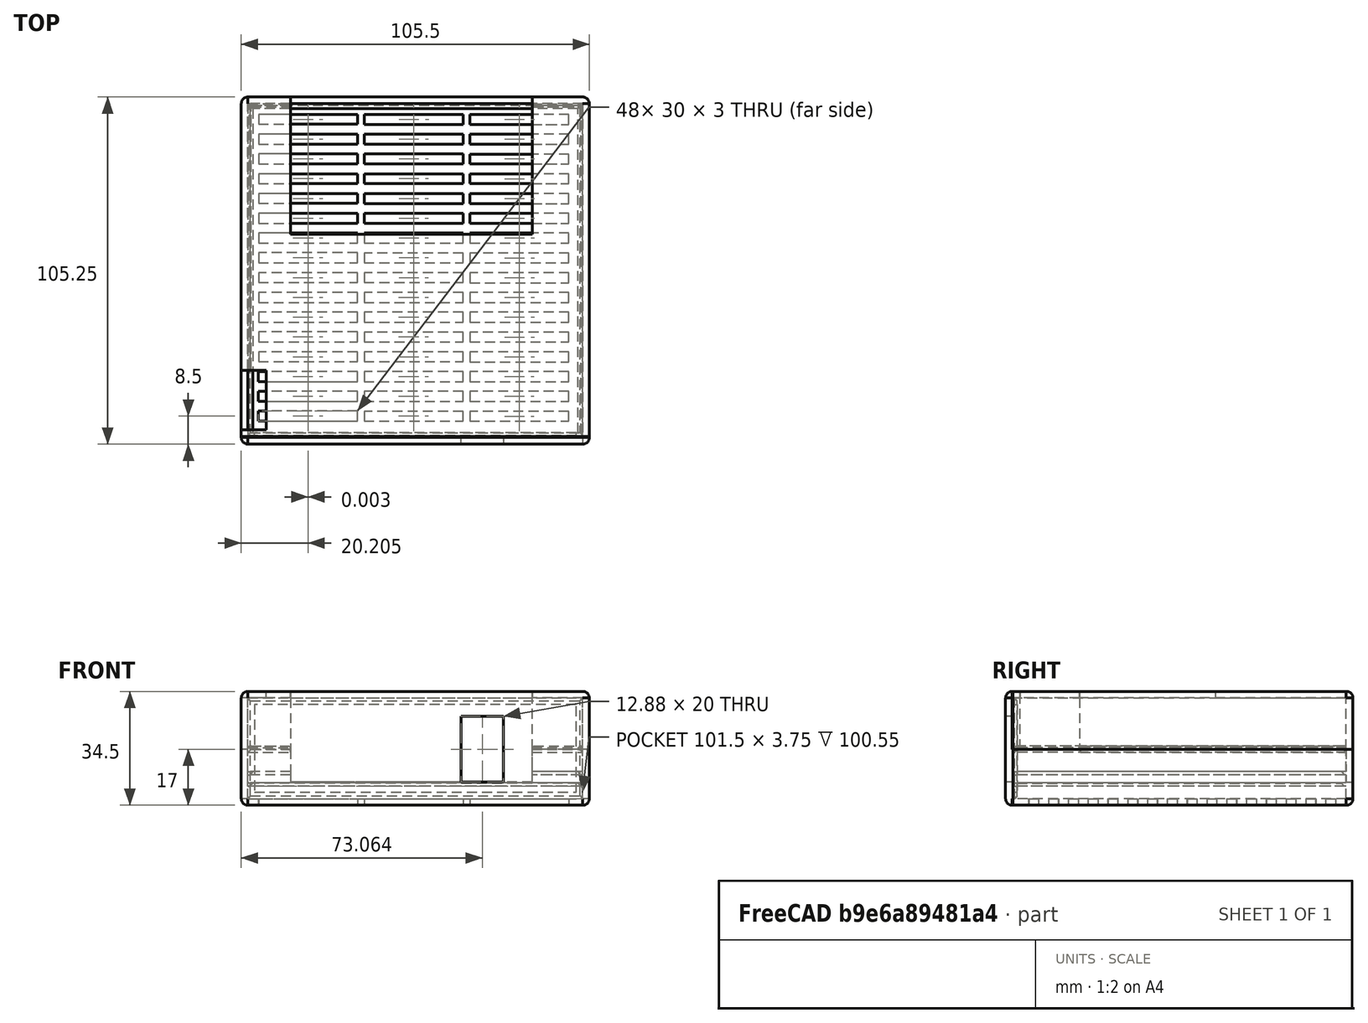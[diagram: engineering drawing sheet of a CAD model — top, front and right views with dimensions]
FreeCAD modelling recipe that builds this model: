
FCSTD DOCUMENT  (FreeCAD 2021.1015R24301 +4280 (Git))
Label: Box
License: All rights reserved
objects: Sketcher::SketchObject×9, PartDesign::SubShapeBinder×6, PartDesign::Pad×5, PartDesign::Pocket×4, PartDesign::Chamfer×3, PartDesign::Body×3, Mesh::Feature×3, PartDesign::Thickness×2, PartDesign::Boolean×2, PartDesign::Solid×2, Mesh::FeatureCustom×1, Spreadsheet::Sheet×1, PartDesign::LinearPattern×1, PartDesign::Split×1
note: 71 computed .brp shape members not serialized (recipe doc carries the construction recipe); baked Part::Feature solids carry a one-line shape summary decoded from their .brp

FEATURE [Mesh::FeatureCustom] OBJ_PCB_BanFlow
  Placement = pos=(-1025.77,1010.73,0) rot=(0,0,1;0rad)
FEATURE [Sketcher::SketchObject] Sketch
  AttachmentOffset = pos=(-0.25,0,-5) rot=(0,0,1;0rad)
  FullyConstrained = true
  MapMode = 5
  Placement = pos=(-0.25,0,-5) rot=(0,0,1;0rad)
  Support = -> [XY_Plane]
  expr: AttachmentOffset.Base.x = -<<Parameters>>.clearance
  expr: AttachmentOffset.Base.z = -<<Parameters>>.PCBLowClearance
  expr: Constraints[10] = <<Parameters>>.PCBwidth + 2 * <<Parameters>>.clearance
  expr: Constraints[9] = <<Parameters>>.PCBwidth + <<Parameters>>.clearance
  sketch-geometry (4):
    g0: LineSegment StartX=0 StartY=0 StartZ=0 EndX=101.5 EndY=0 EndZ=0
    g1: LineSegment StartX=101.5 StartY=0 StartZ=0 EndX=101.5 EndY=101.25 EndZ=0
    g2: LineSegment StartX=101.5 StartY=101.25 StartZ=0 EndX=0 EndY=101.25 EndZ=0
    g3: LineSegment StartX=0 StartY=101.25 StartZ=0 EndX=0 EndY=0 EndZ=0
  constraints (11):
    c: Coincident(g0,g1)
    c: Coincident(g1,g2)
    c: Coincident(g2,g3)
    c: Coincident(g3,g0)
    c: Horizontal(g0)
    c: Horizontal(g2)
    c: Vertical(g1)
    c: Vertical(g3)
    c: Coincident(g0,g-1)
    c: DistanceY(g1,g1) = 101.25
    c: DistanceX(g0,g0) = 101.5
FEATURE [PartDesign::Pad] Pad
  AddSubType = 0
  CheckUpToFaceLimits = true
  ClaimChildren = false
  Direction = (1,1,1)
  Fit = 0
  FitJoin = 0
  InnerFit = 0
  InnerFitJoin = 0
  InnerTaperAngle = 0
  InnerTaperAngleRev = 0
  Length = 30.5
  Length2 = 100
  Linearize = true
  NewSolid = false
  Profile = -> Sketch
  Suppress = false
  Type = 0
  _ProfileBasedVersion = 1
  expr: Length = <<Parameters>>.CaseInsideHeight
FEATURE [PartDesign::Thickness] Thickness
  AddSubType = 0
  Base = -> Pad [Face1]
  BaseFeature = -> Pad
  Intersection = false
  Join = 0
  Mode = 0
  NewSolid = false
  SupportTransform = false
  Suppress = false
  Value = 2
  expr: Value = <<Parameters>>.CaseThickness
FEATURE [Spreadsheet::Sheet] Spreadsheet  label="Parameters"
  PythonMode = false
  cells = A1='clearance; B1(clearance)=0.25; C1='mm; A2='PCB; B2(PCBwidth)=101; C2='mm; A3='PCBLowClearance; B3(PCBLowClearance)=5; C3='mm; A4='PCBHighClearance; B4(PCBHighClearance)=22; C4='mm; A5=PCB thickness; B5(PCBThickness)=3; C5='mm; A6=Case Thickness; B6(CaseThickness)=2; C6='mm; A7=Case inside height; B7(CaseInsideHeight)==PCBThickness + PCBLowClearance + PCBHighClearance + clearance * 2; C7='mm; D7=Clearance is included for PCB holder rails; A8='ShelfWidth; B8(ShelfWidth)=1.5; C8='mm; A9='ShelfThickness; B9(ShelfThickness)=1; C9='mm
FEATURE [PartDesign::SubShapeBinder] Binder  label="Binder(Thickness)..."
  BindCopyOnChange = 0
  BindMode = 0
  ClaimChildren = false
  Context = -> Body001 [Binder.]
  FillStyle = 0
  Fuse = false
  MakeFace = true
  PartialLoad = false
  Relative = true
  Support = -> [Body[Thickness.Edge12,Thickness.Edge8,Thickness.Edge11,Thickness.Edge1]]
  _Version = 8
FEATURE [PartDesign::Pad] Pad001
  AddSubType = 0
  CheckUpToFaceLimits = true
  ClaimChildren = false
  Direction = (1,1,1)
  Fit = 0
  FitJoin = 0
  InnerFit = 0
  InnerFitJoin = 0
  InnerTaperAngle = 0
  InnerTaperAngleRev = 0
  Length = 0.25
  Length2 = 100
  Linearize = true
  NewSolid = false
  Profile = -> Binder
  Suppress = false
  Type = 0
  _ProfileBasedVersion = 1
  expr: Length = <<Parameters>>.clearance
FEATURE [PartDesign::Thickness] Thickness001
  AddSubType = 0
  Base = -> Pad001 [Face6]
  BaseFeature = -> Pad001
  Intersection = false
  Join = 0
  Mode = 0
  NewSolid = false
  SupportTransform = false
  Suppress = false
  Value = 2
  expr: Value = <<Parameters>>.CaseThickness
FEATURE [Sketcher::SketchObject] Sketch001
  AttachmentOffset = pos=(-0.5,0,-0.25) rot=(0,0,1;0rad)
  FullyConstrained = true
  MapMode = 5
  Placement = pos=(-0.5,0,-0.25) rot=(0,0,1;0rad)
  Support = -> [XY_Plane]
  expr: AttachmentOffset.Base.x = -<<Parameters>>.clearance * 2
  expr: AttachmentOffset.Base.z = -<<Parameters>>.clearance
  expr: Constraints[19] = <<Parameters>>.ShelfWidth + <<Parameters>>.clearance
  expr: Constraints[20] = <<Parameters>>.PCBwidth + 2 * <<Parameters>>.clearance
  expr: Constraints[21] = <<Parameters>>.ShelfWidth + <<Parameters>>.clearance
  expr: Constraints[22] = <<Parameters>>.PCBwidth + <<Parameters>>.clearance * 4
  sketch-geometry (8):
    g0: LineSegment StartX=0 StartY=0 StartZ=0 EndX=0 EndY=101.5 EndZ=0
    g1: LineSegment StartX=0 StartY=101.5 StartZ=0 EndX=102 EndY=101.5 EndZ=0
    g2: LineSegment StartX=102 StartY=101.5 StartZ=0 EndX=102 EndY=0 EndZ=0
    g3: LineSegment StartX=102 StartY=3e-15 StartZ=0 EndX=100.25 EndY=3e-15 EndZ=0
    g4: LineSegment StartX=100.25 StartY=3e-15 StartZ=0 EndX=100.25 EndY=99.75 EndZ=0
    g5: LineSegment StartX=100.25 StartY=99.75 StartZ=0 EndX=1.75 EndY=99.75 EndZ=0
    g6: LineSegment StartX=1.75 StartY=99.75 StartZ=0 EndX=1.75 EndY=0 EndZ=0
    g7: LineSegment StartX=1.75 StartY=0 StartZ=0 EndX=0 EndY=0 EndZ=0
  constraints (23):
    c: Coincident(g0,g-1)
    c: PointOnObject(g0,g-2)
    c: Coincident(g1,g0)
    c: Horizontal(g1)
    c: Vertical(g2)
    c: Horizontal(g3)
    c: Coincident(g4,g3)
    c: Vertical(g4)
    c: Horizontal(g5)
    c: Coincident(g6,g5)
    c: Vertical(g6)
    c: Coincident(g7,g6)
    c: Coincident(g7,g0)
    c: Horizontal(g7)
    c: Equal(g7,g3)
    c: Equal(g6,g4)
    c: Coincident(g5,g4)
    c: Coincident(g3,g2)
    c: Coincident(g2,g1)
    c: DistanceY(g4,g1) = 1.75
    c: DistanceY(g0,g0) = 101.5
    c: DistanceX(g7,g7) = 1.75
    c: DistanceX(g1,g1) = 102
FEATURE [PartDesign::Pad] Pad002
  AddSubType = 0
  BaseFeature = -> Thickness
  CheckUpToFaceLimits = true
  ClaimChildren = false
  Direction = (1,1,1)
  Fit = 0
  FitJoin = 0
  InnerFit = 0
  InnerFitJoin = 0
  InnerTaperAngle = 0
  InnerTaperAngleRev = 0
  Length = 1
  Length2 = 100
  Linearize = true
  NewSolid = false
  Profile = -> Sketch001
  Reversed = true
  Suppress = false
  Type = 0
  _ProfileBasedVersion = 1
  expr: Length = <<Parameters>>.ShelfThickness
FEATURE [PartDesign::LinearPattern] LinearPattern
  AddSubType = 0
  BaseFeature = -> Pad002
  CopyShape = false
  Direction = -> Sketch001 [N_Axis]
  Length = 3.5
  NewSolid = false
  Occurrences = 2
  OriginalSubs = -> [Pad002]
  Originals = -> [Pad002]
  ParallelTransform = true
  SubTransform = true
  Suppress = false
  _Version = 3
  expr: Length = <<Parameters>>.PCBThickness + 2 * <<Parameters>>.clearance
FEATURE [Sketcher::SketchObject] Sketch002
  AttachmentOffset = pos=(0,0,10) rot=(0,0,1;0rad)
  FullyConstrained = false
  MapMode = 5
  Placement = pos=(0,0,10) rot=(0,0,1;0rad)
  Support = -> [XY_Plane]
  sketch-geometry (4):
    g0: LineSegment StartX=-6.24338 StartY=2.38313 StartZ=0 EndX=5.37009 EndY=2.38313 EndZ=0
    g1: LineSegment StartX=5.37009 StartY=2.38313 StartZ=0 EndX=5.37009 EndY=20.3657 EndZ=0
    g2: LineSegment StartX=5.37009 StartY=20.3657 StartZ=0 EndX=-6.24338 EndY=20.3657 EndZ=0
    g3: LineSegment StartX=-6.24338 StartY=20.3657 StartZ=0 EndX=-6.24338 EndY=2.38313 EndZ=0
  constraints (8):
    c: Coincident(g0,g1)
    c: Coincident(g1,g2)
    c: Coincident(g2,g3)
    c: Coincident(g3,g0)
    c: Horizontal(g0)
    c: Horizontal(g2)
    c: Vertical(g1)
    c: Vertical(g3)
FEATURE [PartDesign::Pocket] Pocket
  AddSubType = 1
  BaseFeature = -> LinearPattern
  CheckUpToFaceLimits = true
  ClaimChildren = false
  Fit = 0
  FitJoin = 0
  InnerFit = 0
  InnerFitJoin = 0
  InnerTaperAngle = 0
  InnerTaperAngleRev = 0
  Length = 5
  Length2 = 100
  Linearize = true
  NewSolid = false
  Profile = -> Sketch002
  Reversed = true
  Suppress = false
  Type = 1
  _ProfileBasedVersion = 1
  _Version = 1
FEATURE [Sketcher::SketchObject] Sketch003
  FullyConstrained = false
  MapMode = 5
  Support = -> [XY_Plane]
  sketch-geometry (4):
    g0: LineSegment StartX=12.6327 StartY=103.802 StartZ=0 EndX=85.9095 EndY=103.802 EndZ=0
    g1: LineSegment StartX=85.9095 StartY=103.802 StartZ=0 EndX=85.9095 EndY=61.6576 EndZ=0
    g2: LineSegment StartX=85.9095 StartY=61.6576 StartZ=0 EndX=12.6327 EndY=61.6576 EndZ=0
    g3: LineSegment StartX=12.6327 StartY=61.6576 StartZ=0 EndX=12.6327 EndY=103.802 EndZ=0
  constraints (8):
    c: Coincident(g0,g1)
    c: Coincident(g1,g2)
    c: Coincident(g2,g3)
    c: Coincident(g3,g0)
    c: Horizontal(g0)
    c: Horizontal(g2)
    c: Vertical(g1)
    c: Vertical(g3)
FEATURE [PartDesign::Pocket] Pocket001
  AddSubType = 1
  BaseFeature = -> Pocket
  CheckUpToFaceLimits = true
  ClaimChildren = false
  Fit = 0
  FitJoin = 0
  InnerFit = 0
  InnerFitJoin = 0
  InnerTaperAngle = 0
  InnerTaperAngleRev = 0
  Length = 5
  Length2 = 100
  Linearize = true
  NewSolid = false
  Profile = -> Sketch003
  Reversed = true
  Suppress = false
  Type = 1
  _ProfileBasedVersion = 1
  _Version = 1
FEATURE [Sketcher::SketchObject] Sketch005
  FullyConstrained = false
  MapMode = 5
  Support = -> [XY_Plane001]
  sketch-geometry (4):
    g0: LineSegment StartX=64.3744 StartY=20.9694 StartZ=0 EndX=77.2533 EndY=20.9694 EndZ=0
    g1: LineSegment StartX=77.2533 StartY=20.9694 StartZ=0 EndX=77.2533 EndY=-4.03701 EndZ=0
    g2: LineSegment StartX=77.2533 StartY=-4.03701 StartZ=0 EndX=64.3744 EndY=-4.03701 EndZ=0
    g3: LineSegment StartX=64.3744 StartY=-4.03701 StartZ=0 EndX=64.3744 EndY=20.9694 EndZ=0
  constraints (8):
    c: Coincident(g0,g1)
    c: Coincident(g1,g2)
    c: Coincident(g2,g3)
    c: Coincident(g3,g0)
    c: Horizontal(g0)
    c: Horizontal(g2)
    c: Vertical(g1)
    c: Vertical(g3)
FEATURE [PartDesign::Pocket] Pocket002
  AddSubType = 1
  BaseFeature = -> Thickness001
  CheckUpToFaceLimits = true
  ClaimChildren = false
  Fit = 0
  FitJoin = 0
  InnerFit = 0
  InnerFitJoin = 0
  InnerTaperAngle = 0
  InnerTaperAngleRev = 0
  Length = 20
  Length2 = 100
  Linearize = true
  NewSolid = false
  Profile = -> Sketch005
  Reversed = true
  Suppress = false
  Type = 0
  _ProfileBasedVersion = 1
  _Version = 1
FEATURE [Sketcher::SketchObject] Sketch006
  AttachmentOffset = pos=(0,0,10) rot=(0,0,1;0rad)
  FullyConstrained = false
  MapMode = 5
  Placement = pos=(0,0,10) rot=(0,0,1;0rad)
  Support = -> [XY_Plane]
  sketch-geometry (4):
    g0: LineSegment StartX=-6.43563 StartY=105.494 StartZ=0 EndX=106.904 EndY=105.494 EndZ=0
    g1: LineSegment StartX=106.904 StartY=105.494 StartZ=0 EndX=106.904 EndY=-7.55383 EndZ=0
    g2: LineSegment StartX=106.904 StartY=-7.55383 StartZ=0 EndX=-6.43563 EndY=-7.55383 EndZ=0
    g3: LineSegment StartX=-6.43563 StartY=-7.55383 StartZ=0 EndX=-6.43563 EndY=105.494 EndZ=0
  constraints (8):
    c: Coincident(g0,g1)
    c: Coincident(g1,g2)
    c: Coincident(g2,g3)
    c: Coincident(g3,g0)
    c: Horizontal(g0)
    c: Horizontal(g2)
    c: Vertical(g1)
    c: Vertical(g3)
FEATURE [PartDesign::SubShapeBinder] Binder001  label="Binder001(Sketch006)"
  BindCopyOnChange = 0
  BindMode = 0
  ClaimChildren = false
  Context = -> Body [Binder001.]
  FillStyle = 0
  Fuse = false
  MakeFace = true
  PartialLoad = false
  Relative = true
  Support = -> [Sketch006]
  _Version = 8
FEATURE [Sketcher::SketchObject] Sketch007
  AttachmentOffset = pos=(0,0,9) rot=(0,0,1;0rad)
  FullyConstrained = false
  MapMode = 5
  Placement = pos=(0,0,9) rot=(0,0,1;0rad)
  Support = -> [XY_Plane]
  expr: Constraints[29] = <<Parameters>>.clearance
  expr: Constraints[30] = <<Parameters>>.PCBwidth + <<Parameters>>.clearance
  expr: Constraints[32] = <<Parameters>>.PCBwidth + <<Parameters>>.clearance
  sketch-geometry (12):
    g0: LineSegment StartX=0.75 StartY=20.7074 StartZ=0 EndX=0.75 EndY=100.25 EndZ=0
    g1: LineSegment StartX=0.75 StartY=100.25 StartZ=0 EndX=12.6277 EndY=100.25 EndZ=0
    g2: LineSegment StartX=12.6277 StartY=100.25 StartZ=0 EndX=12.6277 EndY=101.25 EndZ=0
    g3: LineSegment StartX=85.9129 StartY=101.25 StartZ=0 EndX=85.9129 EndY=100.25 EndZ=0
    g4: LineSegment StartX=85.9129 StartY=100.25 StartZ=0 EndX=100.25 EndY=100.25 EndZ=0
    g5: LineSegment StartX=100.25 StartY=100.25 StartZ=0 EndX=100.25 EndY=0 EndZ=0
    g6: LineSegment StartX=0.75 StartY=20.7074 StartZ=0 EndX=-0.25 EndY=20.7074 EndZ=0
    g7: LineSegment StartX=-0.25 StartY=20.7074 StartZ=0 EndX=-0.25 EndY=101.25 EndZ=0
    g8: LineSegment StartX=-0.25 StartY=101.25 StartZ=0 EndX=12.6277 EndY=101.25 EndZ=0
    g9: LineSegment StartX=85.9129 StartY=101.25 StartZ=0 EndX=101.25 EndY=101.25 EndZ=0
    g10: LineSegment StartX=101.25 StartY=101.25 StartZ=0 EndX=101.25 EndY=0 EndZ=0
    g11: LineSegment StartX=101.25 StartY=0 StartZ=0 EndX=100.25 EndY=0 EndZ=0
  constraints (33):
    c: Vertical(g0)
    c: Coincident(g1,g0)
    c: Horizontal(g1)
    c: Coincident(g2,g1)
    c: Vertical(g2)
    c: Vertical(g3)
    c: Horizontal(g4)
    c: Coincident(g5,g4)
    c: Vertical(g5)
    c: Equal(g3,g2)
    c: Coincident(g4,g3)
    c: Coincident(g6,g0)
    c: Horizontal(g6)
    c: Coincident(g7,g6)
    c: Vertical(g7)
    c: Coincident(g8,g7)
    c: Coincident(g8,g2)
    c: Horizontal(g8)
    c: Coincident(g9,g3)
    c: Horizontal(g9)
    c: Coincident(g10,g9)
    c: Vertical(g10)
    c: Coincident(g11,g10)
    c: Coincident(g11,g5)
    c: Horizontal(g11)
    c: Equal(g6,g11)
    c: Equal(g11,g3)
    c: DistanceY(g2,g3) = 0
    c: DistanceX(g6,g6) = 1
    c: DistanceX(g6,g-1) = 0.25
    c: DistanceX(g-1,g10) = 101.25
    c: PointOnObject(g10,g-1)
    c: DistanceY(g10,g10) = 101.25
FEATURE [PartDesign::Pad] Pad003
  AddSubType = 0
  CheckUpToFaceLimits = true
  ClaimChildren = false
  Direction = (1,1,1)
  Fit = 0
  FitJoin = 0
  InnerFit = 0
  InnerFitJoin = 0
  InnerTaperAngle = 0
  InnerTaperAngleRev = 0
  Length = 2
  Length2 = 100
  Linearize = true
  NewSolid = false
  Profile = -> Sketch007
  Suppress = false
  Type = 0
  _ProfileBasedVersion = 1
FEATURE [PartDesign::SubShapeBinder] Binder002  label="Binder002(Split_i0)..."
  BindCopyOnChange = 0
  BindMode = 0
  ClaimChildren = false
  Context = -> Body003 [Binder002.]
  FillStyle = 0
  Fuse = true
  MakeFace = true
  PartialLoad = false
  Relative = true
  Support = -> [Body[Split_i0.],Pad003]
  _Version = 8
FEATURE [PartDesign::SubShapeBinder] Reference002  label="Reference002(Pad003)"
  BindCopyOnChange = 0
  BindMode = 0
  ClaimChildren = false
  Context = -> Body003 [Reference002.]
  FillStyle = 0
  Fuse = false
  MakeFace = true
  PartialLoad = false
  Relative = true
  Support = -> [Pad003]
  _Version = 8
FEATURE [PartDesign::SubShapeBinder] Reference003  label="Reference003(*Split_i0...)"
  BindCopyOnChange = 0
  BindMode = 0
  ClaimChildren = false
  Context = -> Body003 [Reference003.]
  FillStyle = 0
  Fuse = false
  MakeFace = true
  PartialLoad = false
  Relative = true
  Support = -> [Binder002]
  _Version = 8
FEATURE [PartDesign::Boolean] Boolean
  ExportMode = 0
  Group = -> [Reference002,Reference003]
  NewSolid = true
  Suppress = false
  Type = 0
  _ExportChildren = -> [Reference002,Reference003]
  _GroupVersion = 1
FEATURE [Sketcher::SketchObject] Sketch008
  ExternalGeometry = -> [Pocket002]
  FullyConstrained = true
  MapMode = 5
  Placement = pos=(0,0,0) rot=(0,0.707107,0.707107;3.14159rad)
  Support = -> [Pocket002]
  sketch-geometry (4):
    g0: LineSegment StartX=-99.25 StartY=23.5 StartZ=0 EndX=-1.75 EndY=23.5 EndZ=0
    g1: LineSegment StartX=-1.75 StartY=23.5 StartZ=0 EndX=-1.75 EndY=-3 EndZ=0
    g2: LineSegment StartX=-1.75 StartY=-3 StartZ=0 EndX=-99.25 EndY=-3 EndZ=0
    g3: LineSegment StartX=-99.25 StartY=-3 StartZ=0 EndX=-99.25 EndY=23.5 EndZ=0
  constraints (12):
    c: Coincident(g0,g1)
    c: Coincident(g1,g2)
    c: Coincident(g2,g3)
    c: Coincident(g3,g0)
    c: Horizontal(g0)
    c: Horizontal(g2)
    c: Vertical(g1)
    c: Vertical(g3)
    c: DistanceY(g0,g-6) = 2
    c: DistanceX(g0,g-6) = 2
    c: DistanceY(g-5,g2) = 2
    c: DistanceX(g-5,g2) = 2
FEATURE [PartDesign::Pad] Pad004
  AddSubType = 0
  BaseFeature = -> Pocket002
  CheckUpToFaceLimits = true
  ClaimChildren = false
  Direction = (1,1,1)
  Fit = 0
  FitJoin = 0
  InnerFit = 0
  InnerFitJoin = 0
  InnerTaperAngle = 0
  InnerTaperAngleRev = 0
  Length = 1.5
  Length2 = 100
  Linearize = true
  NewSolid = false
  Profile = -> Sketch008
  Suppress = false
  Type = 0
  _ProfileBasedVersion = 1
FEATURE [PartDesign::Chamfer] Chamfer
  AddSubType = 0
  Angle = 45
  Base = -> Pad004 [Edge25,Edge26,Edge27,Edge28]
  BaseFeature = -> Pad004
  ChamferType = 0
  FlipDirection = false
  NewSolid = false
  Size = 0.8
  Size2 = 1
  SupportTransform = false
  Suppress = false
FEATURE [PartDesign::Body] Body001  label="SideDoor"
  AutoGroupSolids = false
  ExportMode = 0
  Group = -> [Binder,Pad001,Thickness001,Sketch005,Pocket002,Sketch008,Pad004,Chamfer]
  Origin = -> Origin001
  Tip = -> Chamfer
  _ExportChildren = -> [Pad001,Thickness001,Pocket002,Pad004,Chamfer]
  _GroupVersion = 1
FEATURE [PartDesign::SubShapeBinder] Reference  label="Reference(SideDoor)"
  BindCopyOnChange = 0
  BindMode = 0
  ClaimChildren = false
  Context = -> Body003 [Reference.]
  FillStyle = 0
  Fuse = false
  MakeFace = true
  PartialLoad = false
  Relative = true
  Support = -> [Body001]
  _Version = 8
FEATURE [PartDesign::Boolean] Boolean001
  BaseFeature = -> Boolean
  ExportMode = 0
  Group = -> [Reference]
  NewSolid = false
  Suppress = false
  Type = 1
  _ExportChildren = -> [Reference]
  _GroupVersion = 1
FEATURE [Sketcher::SketchObject] Sketch009
  FullyConstrained = true
  MapMode = 5
  Support = -> [XY_Plane003]
  expr: Constraints[10] = <<Parameters>>.PCBwidth - 3mm
  sketch-geometry (239):
    g0: LineSegment StartX=3 StartY=95 StartZ=0 EndX=33 EndY=95 EndZ=0
    g1: LineSegment StartX=33 StartY=95 StartZ=0 EndX=33 EndY=98 EndZ=0
    g2: LineSegment StartX=33 StartY=98 StartZ=0 EndX=3 EndY=98 EndZ=0
    g3: LineSegment StartX=3 StartY=98 StartZ=0 EndX=3 EndY=95 EndZ=0
    g4: LineSegment StartX=35.033 StartY=94.9839 StartZ=0 EndX=65.033 EndY=94.9839 EndZ=0
    g5: LineSegment StartX=65.033 StartY=94.9839 StartZ=0 EndX=65.033 EndY=97.9839 EndZ=0
    g6: LineSegment StartX=65.033 StartY=97.9839 StartZ=0 EndX=35.033 EndY=97.9839 EndZ=0
    g7: LineSegment StartX=35.033 StartY=97.9839 StartZ=0 EndX=35.033 EndY=94.9839 EndZ=0
    g8: LineSegment [constr] StartX=3 StartY=95 StartZ=0 EndX=35.033 EndY=94.9839 EndZ=0
    g9: LineSegment StartX=67.066 StartY=94.9677 StartZ=0 EndX=97.066 EndY=94.9677 EndZ=0
    g10: LineSegment StartX=97.066 StartY=94.9677 StartZ=0 EndX=97.066 EndY=97.9677 EndZ=0
    g11: LineSegment StartX=97.066 StartY=97.9677 StartZ=0 EndX=67.066 EndY=97.9677 EndZ=0
    g12: LineSegment StartX=67.066 StartY=97.9677 StartZ=0 EndX=67.066 EndY=94.9677 EndZ=0
    g13: LineSegment [constr] StartX=35.033 StartY=94.9839 StartZ=0 EndX=67.066 EndY=94.9677 EndZ=0
    g14: LineSegment StartX=2.99698 StartY=89 StartZ=0 EndX=32.997 EndY=89 EndZ=0
    g15: LineSegment StartX=32.997 StartY=89 StartZ=0 EndX=32.997 EndY=92 EndZ=0
    g16: LineSegment StartX=32.997 StartY=92 StartZ=0 EndX=2.99698 EndY=92 EndZ=0
    g17: LineSegment StartX=2.99698 StartY=92 StartZ=0 EndX=2.99698 EndY=89 EndZ=0
    g18: LineSegment [constr] StartX=3 StartY=95 StartZ=0 EndX=2.99698 EndY=89 EndZ=0
    g19: LineSegment StartX=35.03 StartY=88.9839 StartZ=0 EndX=65.03 EndY=88.9839 EndZ=0
    g20: LineSegment StartX=65.03 StartY=88.9839 StartZ=0 EndX=65.03 EndY=91.9839 EndZ=0
    g21: LineSegment StartX=65.03 StartY=91.9839 StartZ=0 EndX=35.03 EndY=91.9839 EndZ=0
    g22: LineSegment StartX=35.03 StartY=91.9839 StartZ=0 EndX=35.03 EndY=88.9839 EndZ=0
    g23: LineSegment [constr] StartX=2.99698 StartY=89 StartZ=0 EndX=35.03 EndY=88.9839 EndZ=0
    g24: LineSegment StartX=67.0629 StartY=88.9677 StartZ=0 EndX=97.0629 EndY=88.9677 EndZ=0
    g25: LineSegment StartX=97.0629 StartY=88.9677 StartZ=0 EndX=97.0629 EndY=91.9677 EndZ=0
    g26: LineSegment StartX=97.0629 StartY=91.9677 StartZ=0 EndX=67.0629 EndY=91.9677 EndZ=0
    g27: LineSegment StartX=67.0629 StartY=91.9677 StartZ=0 EndX=67.0629 EndY=88.9677 EndZ=0
    g28: LineSegment [constr] StartX=35.03 StartY=88.9839 StartZ=0 EndX=67.0629 EndY=88.9677 EndZ=0
    g29: LineSegment StartX=2.99396 StartY=83 StartZ=0 EndX=32.994 EndY=83 EndZ=0
    g30: LineSegment StartX=32.994 StartY=83 StartZ=0 EndX=32.994 EndY=86 EndZ=0
    g31: LineSegment StartX=32.994 StartY=86 StartZ=0 EndX=2.99396 EndY=86 EndZ=0
    g32: LineSegment StartX=2.99396 StartY=86 StartZ=0 EndX=2.99396 EndY=83 EndZ=0
    g33: LineSegment [constr] StartX=2.99698 StartY=89 StartZ=0 EndX=2.99396 EndY=83 EndZ=0
    g34: LineSegment StartX=35.0269 StartY=82.9839 StartZ=0 EndX=65.0269 EndY=82.9839 EndZ=0
    g35: LineSegment StartX=65.0269 StartY=82.9839 StartZ=0 EndX=65.0269 EndY=85.9839 EndZ=0
    g36: LineSegment StartX=65.0269 StartY=85.9839 StartZ=0 EndX=35.0269 EndY=85.9839 EndZ=0
    g37: LineSegment StartX=35.0269 StartY=85.9839 StartZ=0 EndX=35.0269 EndY=82.9839 EndZ=0
    g38: LineSegment [constr] StartX=2.99396 StartY=83 StartZ=0 EndX=35.0269 EndY=82.9839 EndZ=0
    g39: LineSegment StartX=67.0599 StartY=82.9677 StartZ=0 EndX=97.0599 EndY=82.9677 EndZ=0
    g40: LineSegment StartX=97.0599 StartY=82.9677 StartZ=0 EndX=97.0599 EndY=85.9677 EndZ=0
    g41: LineSegment StartX=97.0599 StartY=85.9677 StartZ=0 EndX=67.0599 EndY=85.9677 EndZ=0
    g42: LineSegment StartX=67.0599 StartY=85.9677 StartZ=0 EndX=67.0599 EndY=82.9677 EndZ=0
    g43: LineSegment [constr] StartX=35.0269 StartY=82.9839 StartZ=0 EndX=67.0599 EndY=82.9677 EndZ=0
    g44: LineSegment StartX=2.99093 StartY=77 StartZ=0 EndX=32.9909 EndY=77 EndZ=0
    g45: LineSegment StartX=32.9909 StartY=77 StartZ=0 EndX=32.9909 EndY=80 EndZ=0
    g46: LineSegment StartX=32.9909 StartY=80 StartZ=0 EndX=2.99093 EndY=80 EndZ=0
    g47: LineSegment StartX=2.99093 StartY=80 StartZ=0 EndX=2.99093 EndY=77 EndZ=0
    g48: LineSegment [constr] StartX=2.99396 StartY=83 StartZ=0 EndX=2.99093 EndY=77 EndZ=0
    g49: LineSegment StartX=35.0239 StartY=76.9839 StartZ=0 EndX=65.0239 EndY=76.9839 EndZ=0
    g50: LineSegment StartX=65.0239 StartY=76.9839 StartZ=0 EndX=65.0239 EndY=79.9839 EndZ=0
    g51: LineSegment StartX=65.0239 StartY=79.9839 StartZ=0 EndX=35.0239 EndY=79.9839 EndZ=0
    g52: LineSegment StartX=35.0239 StartY=79.9839 StartZ=0 EndX=35.0239 EndY=76.9839 EndZ=0
    g53: LineSegment [constr] StartX=2.99093 StartY=77 StartZ=0 EndX=35.0239 EndY=76.9839 EndZ=0
    g54: LineSegment StartX=67.0569 StartY=76.9677 StartZ=0 EndX=97.0569 EndY=76.9677 EndZ=0
    g55: LineSegment StartX=97.0569 StartY=76.9677 StartZ=0 EndX=97.0569 EndY=79.9677 EndZ=0
    g56: LineSegment StartX=97.0569 StartY=79.9677 StartZ=0 EndX=67.0569 EndY=79.9677 EndZ=0
    g57: LineSegment StartX=67.0569 StartY=79.9677 StartZ=0 EndX=67.0569 EndY=76.9677 EndZ=0
    g58: LineSegment [constr] StartX=35.0239 StartY=76.9839 StartZ=0 EndX=67.0569 EndY=76.9677 EndZ=0
    g59: LineSegment StartX=2.98791 StartY=71 StartZ=0 EndX=32.9879 EndY=71 EndZ=0
    g60: LineSegment StartX=32.9879 StartY=71 StartZ=0 EndX=32.9879 EndY=74 EndZ=0
    g61: LineSegment StartX=32.9879 StartY=74 StartZ=0 EndX=2.98791 EndY=74 EndZ=0
    g62: LineSegment StartX=2.98791 StartY=74 StartZ=0 EndX=2.98791 EndY=71 EndZ=0
    g63: LineSegment [constr] StartX=2.99093 StartY=77 StartZ=0 EndX=2.98791 EndY=71 EndZ=0
    g64: LineSegment StartX=35.0209 StartY=70.9839 StartZ=0 EndX=65.0209 EndY=70.9839 EndZ=0
    g65: LineSegment StartX=65.0209 StartY=70.9839 StartZ=0 EndX=65.0209 EndY=73.9839 EndZ=0
    g66: LineSegment StartX=65.0209 StartY=73.9839 StartZ=0 EndX=35.0209 EndY=73.9839 EndZ=0
    g67: LineSegment StartX=35.0209 StartY=73.9839 StartZ=0 EndX=35.0209 EndY=70.9839 EndZ=0
    g68: LineSegment [constr] StartX=2.98791 StartY=71 StartZ=0 EndX=35.0209 EndY=70.9839 EndZ=0
    g69: LineSegment StartX=67.0539 StartY=70.9677 StartZ=0 EndX=97.0539 EndY=70.9677 EndZ=0
    g70: LineSegment StartX=97.0539 StartY=70.9677 StartZ=0 EndX=97.0539 EndY=73.9677 EndZ=0
    g71: LineSegment StartX=97.0539 StartY=73.9677 StartZ=0 EndX=67.0539 EndY=73.9677 EndZ=0
    g72: LineSegment StartX=67.0539 StartY=73.9677 StartZ=0 EndX=67.0539 EndY=70.9677 EndZ=0
    g73: LineSegment [constr] StartX=35.0209 StartY=70.9839 StartZ=0 EndX=67.0539 EndY=70.9677 EndZ=0
    g74: LineSegment StartX=2.98489 StartY=65 StartZ=0 EndX=32.9849 EndY=65 EndZ=0
    g75: LineSegment StartX=32.9849 StartY=65 StartZ=0 EndX=32.9849 EndY=68 EndZ=0
    g76: LineSegment StartX=32.9849 StartY=68 StartZ=0 EndX=2.98489 EndY=68 EndZ=0
    g77: LineSegment StartX=2.98489 StartY=68 StartZ=0 EndX=2.98489 EndY=65 EndZ=0
    g78: LineSegment [constr] StartX=2.98791 StartY=71 StartZ=0 EndX=2.98489 EndY=65 EndZ=0
    g79: LineSegment StartX=35.0179 StartY=64.9839 StartZ=0 EndX=65.0179 EndY=64.9839 EndZ=0
    g80: LineSegment StartX=65.0179 StartY=64.9839 StartZ=0 EndX=65.0179 EndY=67.9839 EndZ=0
    g81: LineSegment StartX=65.0179 StartY=67.9839 StartZ=0 EndX=35.0179 EndY=67.9839 EndZ=0
    g82: LineSegment StartX=35.0179 StartY=67.9839 StartZ=0 EndX=35.0179 EndY=64.9839 EndZ=0
    g83: LineSegment [constr] StartX=2.98489 StartY=65 StartZ=0 EndX=35.0179 EndY=64.9839 EndZ=0
    g84: LineSegment StartX=67.0509 StartY=64.9677 StartZ=0 EndX=97.0509 EndY=64.9677 EndZ=0
    g85: LineSegment StartX=97.0509 StartY=64.9677 StartZ=0 EndX=97.0509 EndY=67.9677 EndZ=0
    g86: LineSegment StartX=97.0509 StartY=67.9677 StartZ=0 EndX=67.0509 EndY=67.9677 EndZ=0
    g87: LineSegment StartX=67.0509 StartY=67.9677 StartZ=0 EndX=67.0509 EndY=64.9677 EndZ=0
    g88: LineSegment [constr] StartX=35.0179 StartY=64.9839 StartZ=0 EndX=67.0509 EndY=64.9677 EndZ=0
    g89: LineSegment StartX=2.98187 StartY=59 StartZ=0 EndX=32.9819 EndY=59 EndZ=0
    g90: LineSegment StartX=32.9819 StartY=59 StartZ=0 EndX=32.9819 EndY=62 EndZ=0
    g91: LineSegment StartX=32.9819 StartY=62 StartZ=0 EndX=2.98187 EndY=62 EndZ=0
    g92: LineSegment StartX=2.98187 StartY=62 StartZ=0 EndX=2.98187 EndY=59 EndZ=0
    g93: LineSegment [constr] StartX=2.98489 StartY=65 StartZ=0 EndX=2.98187 EndY=59 EndZ=0
    g94: LineSegment StartX=35.0149 StartY=58.9839 StartZ=0 EndX=65.0149 EndY=58.9839 EndZ=0
    g95: LineSegment StartX=65.0149 StartY=58.9839 StartZ=0 EndX=65.0149 EndY=61.9839 EndZ=0
    g96: LineSegment StartX=65.0149 StartY=61.9839 StartZ=0 EndX=35.0149 EndY=61.9839 EndZ=0
    g97: LineSegment StartX=35.0149 StartY=61.9839 StartZ=0 EndX=35.0149 EndY=58.9839 EndZ=0
    g98: LineSegment [constr] StartX=2.98187 StartY=59 StartZ=0 EndX=35.0149 EndY=58.9839 EndZ=0
    g99: LineSegment StartX=67.0478 StartY=58.9677 StartZ=0 EndX=97.0478 EndY=58.9677 EndZ=0
    g100: LineSegment StartX=97.0478 StartY=58.9677 StartZ=0 EndX=97.0478 EndY=61.9677 EndZ=0
    g101: LineSegment StartX=97.0478 StartY=61.9677 StartZ=0 EndX=67.0478 EndY=61.9677 EndZ=0
    g102: LineSegment StartX=67.0478 StartY=61.9677 StartZ=0 EndX=67.0478 EndY=58.9677 EndZ=0
    g103: LineSegment [constr] StartX=35.0149 StartY=58.9839 StartZ=0 EndX=67.0478 EndY=58.9677 EndZ=0
    g104: LineSegment StartX=2.97884 StartY=53 StartZ=0 EndX=32.9788 EndY=53 EndZ=0
    g105: LineSegment StartX=32.9788 StartY=53 StartZ=0 EndX=32.9788 EndY=56 EndZ=0
    g106: LineSegment StartX=32.9788 StartY=56 StartZ=0 EndX=2.97884 EndY=56 EndZ=0
    g107: LineSegment StartX=2.97884 StartY=56 StartZ=0 EndX=2.97884 EndY=53 EndZ=0
    g108: LineSegment [constr] StartX=2.98187 StartY=59 StartZ=0 EndX=2.97884 EndY=53 EndZ=0
    g109: LineSegment StartX=35.0118 StartY=52.9839 StartZ=0 EndX=65.0118 EndY=52.9839 EndZ=0
    g110: LineSegment StartX=65.0118 StartY=52.9839 StartZ=0 EndX=65.0118 EndY=55.9839 EndZ=0
    g111: LineSegment StartX=65.0118 StartY=55.9839 StartZ=0 EndX=35.0118 EndY=55.9839 EndZ=0
    g112: LineSegment StartX=35.0118 StartY=55.9839 StartZ=0 EndX=35.0118 EndY=52.9839 EndZ=0
    g113: LineSegment [constr] StartX=2.97884 StartY=53 StartZ=0 EndX=35.0118 EndY=52.9839 EndZ=0
    g114: LineSegment StartX=67.0448 StartY=52.9677 StartZ=0 EndX=97.0448 EndY=52.9677 EndZ=0
    g115: LineSegment StartX=97.0448 StartY=52.9677 StartZ=0 EndX=97.0448 EndY=55.9677 EndZ=0
    g116: LineSegment StartX=97.0448 StartY=55.9677 StartZ=0 EndX=67.0448 EndY=55.9677 EndZ=0
    g117: LineSegment StartX=67.0448 StartY=55.9677 StartZ=0 EndX=67.0448 EndY=52.9677 EndZ=0
    g118: LineSegment [constr] StartX=35.0118 StartY=52.9839 StartZ=0 EndX=67.0448 EndY=52.9677 EndZ=0
    g119: LineSegment StartX=2.97582 StartY=47 StartZ=0 EndX=32.9758 EndY=47 EndZ=0
    g120: LineSegment StartX=32.9758 StartY=47 StartZ=0 EndX=32.9758 EndY=50 EndZ=0
    g121: LineSegment StartX=32.9758 StartY=50 StartZ=0 EndX=2.97582 EndY=50 EndZ=0
    g122: LineSegment StartX=2.97582 StartY=50 StartZ=0 EndX=2.97582 EndY=47 EndZ=0
    g123: LineSegment [constr] StartX=2.97884 StartY=53 StartZ=0 EndX=2.97582 EndY=47 EndZ=0
    g124: LineSegment StartX=35.0088 StartY=46.9839 StartZ=0 EndX=65.0088 EndY=46.9839 EndZ=0
    g125: LineSegment StartX=65.0088 StartY=46.9839 StartZ=0 EndX=65.0088 EndY=49.9839 EndZ=0
    g126: LineSegment StartX=65.0088 StartY=49.9839 StartZ=0 EndX=35.0088 EndY=49.9839 EndZ=0
    g127: LineSegment StartX=35.0088 StartY=49.9839 StartZ=0 EndX=35.0088 EndY=46.9839 EndZ=0
    g128: LineSegment [constr] StartX=2.97582 StartY=47 StartZ=0 EndX=35.0088 EndY=46.9839 EndZ=0
    g129: LineSegment StartX=67.0418 StartY=46.9677 StartZ=0 EndX=97.0418 EndY=46.9677 EndZ=0
    g130: LineSegment StartX=97.0418 StartY=46.9677 StartZ=0 EndX=97.0418 EndY=49.9677 EndZ=0
    g131: LineSegment StartX=97.0418 StartY=49.9677 StartZ=0 EndX=67.0418 EndY=49.9677 EndZ=0
    g132: LineSegment StartX=67.0418 StartY=49.9677 StartZ=0 EndX=67.0418 EndY=46.9677 EndZ=0
    g133: LineSegment [constr] StartX=35.0088 StartY=46.9839 StartZ=0 EndX=67.0418 EndY=46.9677 EndZ=0
    g134: LineSegment StartX=2.9728 StartY=41 StartZ=0 EndX=32.9728 EndY=41 EndZ=0
    g135: LineSegment StartX=32.9728 StartY=41 StartZ=0 EndX=32.9728 EndY=44 EndZ=0
    g136: LineSegment StartX=32.9728 StartY=44 StartZ=0 EndX=2.9728 EndY=44 EndZ=0
    g137: LineSegment StartX=2.9728 StartY=44 StartZ=0 EndX=2.9728 EndY=41 EndZ=0
    g138: LineSegment [constr] StartX=2.97582 StartY=47 StartZ=0 EndX=2.9728 EndY=41 EndZ=0
    g139: LineSegment StartX=35.0058 StartY=40.9839 StartZ=0 EndX=65.0058 EndY=40.9839 EndZ=0
    g140: LineSegment StartX=65.0058 StartY=40.9839 StartZ=0 EndX=65.0058 EndY=43.9839 EndZ=0
    g141: LineSegment StartX=65.0058 StartY=43.9839 StartZ=0 EndX=35.0058 EndY=43.9839 EndZ=0
    g142: LineSegment StartX=35.0058 StartY=43.9839 StartZ=0 EndX=35.0058 EndY=40.9839 EndZ=0
    g143: LineSegment [constr] StartX=2.9728 StartY=41 StartZ=0 EndX=35.0058 EndY=40.9839 EndZ=0
    g144: LineSegment StartX=67.0388 StartY=40.9677 StartZ=0 EndX=97.0388 EndY=40.9677 EndZ=0
    g145: LineSegment StartX=97.0388 StartY=40.9677 StartZ=0 EndX=97.0388 EndY=43.9677 EndZ=0
    g146: LineSegment StartX=97.0388 StartY=43.9677 StartZ=0 EndX=67.0388 EndY=43.9677 EndZ=0
    g147: LineSegment StartX=67.0388 StartY=43.9677 StartZ=0 EndX=67.0388 EndY=40.9677 EndZ=0
    g148: LineSegment [constr] StartX=35.0058 StartY=40.9839 StartZ=0 EndX=67.0388 EndY=40.9677 EndZ=0
    g149: LineSegment StartX=2.96978 StartY=35 StartZ=0 EndX=32.9698 EndY=35 EndZ=0
    g150: LineSegment StartX=32.9698 StartY=35 StartZ=0 EndX=32.9698 EndY=38 EndZ=0
    g151: LineSegment StartX=32.9698 StartY=38 StartZ=0 EndX=2.96978 EndY=38 EndZ=0
    g152: LineSegment StartX=2.96978 StartY=38 StartZ=0 EndX=2.96978 EndY=35 EndZ=0
    g153: LineSegment [constr] StartX=2.9728 StartY=41 StartZ=0 EndX=2.96978 EndY=35 EndZ=0
    g154: LineSegment StartX=35.0028 StartY=34.9839 StartZ=0 EndX=65.0028 EndY=34.9839 EndZ=0
    g155: LineSegment StartX=65.0028 StartY=34.9839 StartZ=0 EndX=65.0028 EndY=37.9839 EndZ=0
    g156: LineSegment StartX=65.0028 StartY=37.9839 StartZ=0 EndX=35.0028 EndY=37.9839 EndZ=0
    g157: LineSegment StartX=35.0028 StartY=37.9839 StartZ=0 EndX=35.0028 EndY=34.9839 EndZ=0
    g158: LineSegment [constr] StartX=2.96978 StartY=35 StartZ=0 EndX=35.0028 EndY=34.9839 EndZ=0
    g159: LineSegment StartX=67.0357 StartY=34.9677 StartZ=0 EndX=97.0357 EndY=34.9677 EndZ=0
    g160: LineSegment StartX=97.0357 StartY=34.9677 StartZ=0 EndX=97.0357 EndY=37.9677 EndZ=0
    g161: LineSegment StartX=97.0357 StartY=37.9677 StartZ=0 EndX=67.0357 EndY=37.9677 EndZ=0
    g162: LineSegment StartX=67.0357 StartY=37.9677 StartZ=0 EndX=67.0357 EndY=34.9677 EndZ=0
    g163: LineSegment [constr] StartX=35.0028 StartY=34.9839 StartZ=0 EndX=67.0357 EndY=34.9677 EndZ=0
    g164: LineSegment StartX=2.96675 StartY=29 StartZ=0 EndX=32.9668 EndY=29 EndZ=0
    g165: LineSegment StartX=32.9668 StartY=29 StartZ=0 EndX=32.9668 EndY=32 EndZ=0
    g166: LineSegment StartX=32.9668 StartY=32 StartZ=0 EndX=2.96675 EndY=32 EndZ=0
    g167: LineSegment StartX=2.96675 StartY=32 StartZ=0 EndX=2.96675 EndY=29 EndZ=0
    g168: LineSegment [constr] StartX=2.96978 StartY=35 StartZ=0 EndX=2.96675 EndY=29 EndZ=0
    g169: LineSegment StartX=34.9997 StartY=28.9839 StartZ=0 EndX=64.9997 EndY=28.9839 EndZ=0
    g170: LineSegment StartX=64.9997 StartY=28.9839 StartZ=0 EndX=64.9997 EndY=31.9839 EndZ=0
    g171: LineSegment StartX=64.9997 StartY=31.9839 StartZ=0 EndX=34.9997 EndY=31.9839 EndZ=0
    g172: LineSegment StartX=34.9997 StartY=31.9839 StartZ=0 EndX=34.9997 EndY=28.9839 EndZ=0
    g173: LineSegment [constr] StartX=2.96675 StartY=29 StartZ=0 EndX=34.9997 EndY=28.9839 EndZ=0
    g174: LineSegment StartX=67.0327 StartY=28.9677 StartZ=0 EndX=97.0327 EndY=28.9677 EndZ=0
    g175: LineSegment StartX=97.0327 StartY=28.9677 StartZ=0 EndX=97.0327 EndY=31.9677 EndZ=0
    g176: LineSegment StartX=97.0327 StartY=31.9677 StartZ=0 EndX=67.0327 EndY=31.9677 EndZ=0
    g177: LineSegment StartX=67.0327 StartY=31.9677 StartZ=0 EndX=67.0327 EndY=28.9677 EndZ=0
    g178: LineSegment [constr] StartX=34.9997 StartY=28.9839 StartZ=0 EndX=67.0327 EndY=28.9677 EndZ=0
    g179: LineSegment StartX=2.96373 StartY=23 StartZ=0 EndX=32.9637 EndY=23 EndZ=0
    g180: LineSegment StartX=32.9637 StartY=23 StartZ=0 EndX=32.9637 EndY=26 EndZ=0
    g181: LineSegment StartX=32.9637 StartY=26 StartZ=0 EndX=2.96373 EndY=26 EndZ=0
    g182: LineSegment StartX=2.96373 StartY=26 StartZ=0 EndX=2.96373 EndY=23 EndZ=0
    g183: LineSegment [constr] StartX=2.96675 StartY=29 StartZ=0 EndX=2.96373 EndY=23 EndZ=0
    g184: LineSegment StartX=34.9967 StartY=22.9839 StartZ=0 EndX=64.9967 EndY=22.9839 EndZ=0
    g185: LineSegment StartX=64.9967 StartY=22.9839 StartZ=0 EndX=64.9967 EndY=25.9839 EndZ=0
    g186: LineSegment StartX=64.9967 StartY=25.9839 StartZ=0 EndX=34.9967 EndY=25.9839 EndZ=0
    g187: LineSegment StartX=34.9967 StartY=25.9839 StartZ=0 EndX=34.9967 EndY=22.9839 EndZ=0
    g188: LineSegment [constr] StartX=2.96373 StartY=23 StartZ=0 EndX=34.9967 EndY=22.9839 EndZ=0
    g189: LineSegment StartX=67.0297 StartY=22.9677 StartZ=0 EndX=97.0297 EndY=22.9677 EndZ=0
    g190: LineSegment StartX=97.0297 StartY=22.9677 StartZ=0 EndX=97.0297 EndY=25.9677 EndZ=0
    g191: LineSegment StartX=97.0297 StartY=25.9677 StartZ=0 EndX=67.0297 EndY=25.9677 EndZ=0
    g192: LineSegment StartX=67.0297 StartY=25.9677 StartZ=0 EndX=67.0297 EndY=22.9677 EndZ=0
    g193: LineSegment [constr] StartX=34.9967 StartY=22.9839 StartZ=0 EndX=67.0297 EndY=22.9677 EndZ=0
    g194: LineSegment StartX=2.96071 StartY=17 StartZ=0 EndX=32.9607 EndY=17 EndZ=0
    g195: LineSegment StartX=32.9607 StartY=17 StartZ=0 EndX=32.9607 EndY=20 EndZ=0
    g196: LineSegment StartX=32.9607 StartY=20 StartZ=0 EndX=2.96071 EndY=20 EndZ=0
    g197: LineSegment StartX=2.96071 StartY=20 StartZ=0 EndX=2.96071 EndY=17 EndZ=0
    g198: LineSegment [constr] StartX=2.96373 StartY=23 StartZ=0 EndX=2.96071 EndY=17 EndZ=0
    g199: LineSegment StartX=34.9937 StartY=16.9839 StartZ=0 EndX=64.9937 EndY=16.9839 EndZ=0
    g200: LineSegment StartX=64.9937 StartY=16.9839 StartZ=0 EndX=64.9937 EndY=19.9839 EndZ=0
    g201: LineSegment StartX=64.9937 StartY=19.9839 StartZ=0 EndX=34.9937 EndY=19.9839 EndZ=0
    g202: LineSegment StartX=34.9937 StartY=19.9839 StartZ=0 EndX=34.9937 EndY=16.9839 EndZ=0
    g203: LineSegment [constr] StartX=2.96071 StartY=17 StartZ=0 EndX=34.9937 EndY=16.9839 EndZ=0
    g204: LineSegment StartX=67.0267 StartY=16.9677 StartZ=0 EndX=97.0267 EndY=16.9677 EndZ=0
    g205: LineSegment StartX=97.0267 StartY=16.9677 StartZ=0 EndX=97.0267 EndY=19.9677 EndZ=0
    g206: LineSegment StartX=97.0267 StartY=19.9677 StartZ=0 EndX=67.0267 EndY=19.9677 EndZ=0
    g207: LineSegment StartX=67.0267 StartY=19.9677 StartZ=0 EndX=67.0267 EndY=16.9677 EndZ=0
    g208: LineSegment [constr] StartX=34.9937 StartY=16.9839 StartZ=0 EndX=67.0267 EndY=16.9677 EndZ=0
    g209: LineSegment StartX=2.95769 StartY=11 StartZ=0 EndX=32.9577 EndY=11 EndZ=0
    g210: LineSegment StartX=32.9577 StartY=11 StartZ=0 EndX=32.9577 EndY=14 EndZ=0
    g211: LineSegment StartX=32.9577 StartY=14 StartZ=0 EndX=2.95769 EndY=14 EndZ=0
    g212: LineSegment StartX=2.95769 StartY=14 StartZ=0 EndX=2.95769 EndY=11 EndZ=0
    g213: LineSegment [constr] StartX=2.96071 StartY=17 StartZ=0 EndX=2.95769 EndY=11 EndZ=0
    g214: LineSegment StartX=34.9907 StartY=10.9839 StartZ=0 EndX=64.9907 EndY=10.9839 EndZ=0
    g215: LineSegment StartX=64.9907 StartY=10.9839 StartZ=0 EndX=64.9907 EndY=13.9839 EndZ=0
    g216: LineSegment StartX=64.9907 StartY=13.9839 StartZ=0 EndX=34.9907 EndY=13.9839 EndZ=0
    g217: LineSegment StartX=34.9907 StartY=13.9839 StartZ=0 EndX=34.9907 EndY=10.9839 EndZ=0
    g218: LineSegment [constr] StartX=2.95769 StartY=11 StartZ=0 EndX=34.9907 EndY=10.9839 EndZ=0
    g219: LineSegment StartX=67.0237 StartY=10.9677 StartZ=0 EndX=97.0237 EndY=10.9677 EndZ=0
    g220: LineSegment StartX=97.0237 StartY=10.9677 StartZ=0 EndX=97.0237 EndY=13.9677 EndZ=0
    g221: LineSegment StartX=97.0237 StartY=13.9677 StartZ=0 EndX=67.0237 EndY=13.9677 EndZ=0
    g222: LineSegment StartX=67.0237 StartY=13.9677 StartZ=0 EndX=67.0237 EndY=10.9677 EndZ=0
    g223: LineSegment [constr] StartX=34.9907 StartY=10.9839 StartZ=0 EndX=67.0237 EndY=10.9677 EndZ=0
    g224: LineSegment StartX=2.95466 StartY=5.00001 StartZ=0 EndX=32.9547 EndY=5.00001 EndZ=0
    g225: LineSegment StartX=32.9547 StartY=5.00001 StartZ=0 EndX=32.9547 EndY=8.00001 EndZ=0
    g226: LineSegment StartX=32.9547 StartY=8.00001 StartZ=0 EndX=2.95466 EndY=8.00001 EndZ=0
    g227: LineSegment StartX=2.95466 StartY=8.00001 StartZ=0 EndX=2.95466 EndY=5.00001 EndZ=0
    g228: LineSegment [constr] StartX=2.95769 StartY=11 StartZ=0 EndX=2.95466 EndY=5.00001 EndZ=0
    g229: LineSegment StartX=34.9877 StartY=4.98388 StartZ=0 EndX=64.9877 EndY=4.98388 EndZ=0
    g230: LineSegment StartX=64.9877 StartY=4.98388 StartZ=0 EndX=64.9877 EndY=7.98388 EndZ=0
    g231: LineSegment StartX=64.9877 StartY=7.98388 StartZ=0 EndX=34.9877 EndY=7.98388 EndZ=0
    g232: LineSegment StartX=34.9877 StartY=7.98388 StartZ=0 EndX=34.9877 EndY=4.98388 EndZ=0
    g233: LineSegment [constr] StartX=2.95466 StartY=5.00001 StartZ=0 EndX=34.9877 EndY=4.98388 EndZ=0
    g234: LineSegment StartX=67.0206 StartY=4.96774 StartZ=0 EndX=97.0206 EndY=4.96774 EndZ=0
    g235: LineSegment StartX=97.0206 StartY=4.96774 StartZ=0 EndX=97.0206 EndY=7.96774 EndZ=0
    g236: LineSegment StartX=97.0206 StartY=7.96774 StartZ=0 EndX=67.0206 EndY=7.96774 EndZ=0
    g237: LineSegment StartX=67.0206 StartY=7.96774 StartZ=0 EndX=67.0206 EndY=4.96774 EndZ=0
    g238: LineSegment [constr] StartX=34.9877 StartY=4.98388 StartZ=0 EndX=67.0206 EndY=4.96774 EndZ=0
  constraints (670):
    c: Coincident(g0,g1)
    c: Coincident(g1,g2)
    c: Coincident(g2,g3)
    c: Coincident(g3,g0)
    c: Horizontal(g0)
    c: Horizontal(g2)
    c: Vertical(g1)
    c: Vertical(g3)
    c: DistanceX(g2,g2) = 30
    c: DistanceY(g1,g1) = 3
    c: DistanceY(g-1,g2) = 98
    c: DistanceX(g-1,g0) = 3
    c: Coincident(g4,g5)
    c: Coincident(g5,g6)
    c: Coincident(g6,g7)
    c: Coincident(g7,g4)
    c: Horizontal(g4)
    c: Horizontal(g6)
    c: Vertical(g5)
    c: Vertical(g7)
    c: Equal(g2,g6) = 30
    c: Equal(g1,g5) = 3
    c: Coincident(g0,g8)
    c: Coincident(g4,g8)
    c: Distance(g8) = 32.033
    c: Angle(g8) = -0.000503731
    c: Coincident(g9,g10)
    c: Coincident(g10,g11)
    c: Coincident(g11,g12)
    c: Coincident(g12,g9)
    c: Horizontal(g9)
    c: Horizontal(g11)
    c: Vertical(g10)
    c: Vertical(g12)
    c: Equal(g2,g11) = 30
    c: Equal(g1,g10) = 3
    c: Coincident(g4,g13)
    c: Coincident(g9,g13)
    c: Equal(g8,g13)
    c: Parallel(g13,g8)
    c: Coincident(g14,g15)
    c: Coincident(g15,g16)
    c: Coincident(g16,g17)
    c: Coincident(g17,g14)
    c: Horizontal(g14)
    c: Horizontal(g16)
    c: Vertical(g15)
    c: Vertical(g17)
    c: Equal(g2,g16) = 30
    c: Equal(g1,g15) = 3
    c: Coincident(g0,g18)
    c: Coincident(g14,g18)
    c: Distance(g18) = 6
    c: Perpendicular(g18,g8)
    c: Coincident(g19,g20)
    c: Coincident(g20,g21)
    c: Coincident(g21,g22)
    c: Coincident(g22,g19)
    c: Horizontal(g19)
    c: Horizontal(g21)
    c: Vertical(g20)
    c: Vertical(g22)
    c: Equal(g2,g21) = 30
    c: Equal(g1,g20) = 3
    c: Coincident(g14,g23)
    c: Coincident(g19,g23)
    c: Equal(g8,g23)
    c: Parallel(g23,g8)
    c: Coincident(g24,g25)
    c: Coincident(g25,g26)
    c: Coincident(g26,g27)
    c: Coincident(g27,g24)
    c: Horizontal(g24)
    c: Horizontal(g26)
    c: Vertical(g25)
    c: Vertical(g27)
    c: Equal(g2,g26) = 30
    c: Equal(g1,g25) = 3
    c: Coincident(g19,g28)
    c: Coincident(g24,g28)
    c: Equal(g8,g28)
    c: Parallel(g28,g8)
    c: Coincident(g29,g30)
    c: Coincident(g30,g31)
    c: Coincident(g31,g32)
    c: Coincident(g32,g29)
    c: Horizontal(g29)
    c: Horizontal(g31)
    c: Vertical(g30)
    c: Vertical(g32)
    c: Equal(g2,g31) = 30
    c: Equal(g1,g30) = 3
    c: Coincident(g14,g33)
    c: Coincident(g29,g33)
    c: Equal(g18,g33)
    c: Perpendicular(g33,g8)
    c: Coincident(g34,g35)
    c: Coincident(g35,g36)
    c: Coincident(g36,g37)
    c: Coincident(g37,g34)
    c: Horizontal(g34)
    c: Horizontal(g36)
    c: Vertical(g35)
    c: Vertical(g37)
    c: Equal(g2,g36) = 30
    c: Equal(g1,g35) = 3
    c: Coincident(g29,g38)
    c: Coincident(g34,g38)
    c: Equal(g8,g38)
    c: Parallel(g38,g8)
    c: Coincident(g39,g40)
    c: Coincident(g40,g41)
    c: Coincident(g41,g42)
    c: Coincident(g42,g39)
    c: Horizontal(g39)
    c: Horizontal(g41)
    c: Vertical(g40)
    c: Vertical(g42)
    c: Equal(g2,g41) = 30
    c: Equal(g1,g40) = 3
    c: Coincident(g34,g43)
    c: Coincident(g39,g43)
    c: Equal(g8,g43)
    c: Parallel(g43,g8)
    c: Coincident(g44,g45)
    c: Coincident(g45,g46)
    c: Coincident(g46,g47)
    c: Coincident(g47,g44)
    c: Horizontal(g44)
    c: Horizontal(g46)
    c: Vertical(g45)
    c: Vertical(g47)
    c: Equal(g2,g46) = 30
    c: Equal(g1,g45) = 3
    c: Coincident(g29,g48)
    c: Coincident(g44,g48)
    c: Equal(g18,g48)
    c: Perpendicular(g48,g8)
    c: Coincident(g49,g50)
    c: Coincident(g50,g51)
    c: Coincident(g51,g52)
    c: Coincident(g52,g49)
    c: Horizontal(g49)
    c: Horizontal(g51)
    c: Vertical(g50)
    c: Vertical(g52)
    c: Equal(g2,g51) = 30
    c: Equal(g1,g50) = 3
    c: Coincident(g44,g53)
    c: Coincident(g49,g53)
    c: Equal(g8,g53)
    c: Parallel(g53,g8)
    c: Coincident(g54,g55)
    c: Coincident(g55,g56)
    c: Coincident(g56,g57)
    c: Coincident(g57,g54)
    c: Horizontal(g54)
    c: Horizontal(g56)
    c: Vertical(g55)
    c: Vertical(g57)
    c: Equal(g2,g56) = 30
    c: Equal(g1,g55) = 3
    c: Coincident(g49,g58)
    c: Coincident(g54,g58)
    c: Equal(g8,g58)
    c: Parallel(g58,g8)
    c: Coincident(g59,g60)
    c: Coincident(g60,g61)
    c: Coincident(g61,g62)
    c: Coincident(g62,g59)
    c: Horizontal(g59)
    c: Horizontal(g61)
    c: Vertical(g60)
    c: Vertical(g62)
    c: Equal(g2,g61) = 30
    c: Equal(g1,g60) = 3
    c: Coincident(g44,g63)
    c: Coincident(g59,g63)
    c: Equal(g18,g63)
    c: Perpendicular(g63,g8)
    c: Coincident(g64,g65)
    c: Coincident(g65,g66)
    c: Coincident(g66,g67)
    c: Coincident(g67,g64)
    c: Horizontal(g64)
    c: Horizontal(g66)
    c: Vertical(g65)
    c: Vertical(g67)
    c: Equal(g2,g66) = 30
    c: Equal(g1,g65) = 3
    c: Coincident(g59,g68)
    c: Coincident(g64,g68)
    c: Equal(g8,g68)
    c: Parallel(g68,g8)
    c: Coincident(g69,g70)
    c: Coincident(g70,g71)
    c: Coincident(g71,g72)
    c: Coincident(g72,g69)
    c: Horizontal(g69)
    c: Horizontal(g71)
    c: Vertical(g70)
    c: Vertical(g72)
    c: Equal(g2,g71) = 30
    c: Equal(g1,g70) = 3
    c: Coincident(g64,g73)
    c: Coincident(g69,g73)
    c: Equal(g8,g73)
    c: Parallel(g73,g8)
    c: Coincident(g74,g75)
    c: Coincident(g75,g76)
    c: Coincident(g76,g77)
    c: Coincident(g77,g74)
    c: Horizontal(g74)
    c: Horizontal(g76)
    c: Vertical(g75)
    c: Vertical(g77)
    c: Equal(g2,g76) = 30
    c: Equal(g1,g75) = 3
    c: Coincident(g59,g78)
    c: Coincident(g74,g78)
    c: Equal(g18,g78)
    c: Perpendicular(g78,g8)
    c: Coincident(g79,g80)
    c: Coincident(g80,g81)
    c: Coincident(g81,g82)
    c: Coincident(g82,g79)
    c: Horizontal(g79)
    c: Horizontal(g81)
    c: Vertical(g80)
    c: Vertical(g82)
    c: Equal(g2,g81) = 30
    c: Equal(g1,g80) = 3
    c: Coincident(g74,g83)
    c: Coincident(g79,g83)
    c: Equal(g8,g83)
    c: Parallel(g83,g8)
    c: Coincident(g84,g85)
    c: Coincident(g85,g86)
    c: Coincident(g86,g87)
    c: Coincident(g87,g84)
    c: Horizontal(g84)
    c: Horizontal(g86)
    c: Vertical(g85)
    c: Vertical(g87)
    c: Equal(g2,g86) = 30
    c: Equal(g1,g85) = 3
    c: Coincident(g79,g88)
    c: Coincident(g84,g88)
    c: Equal(g8,g88)
    c: Parallel(g88,g8)
    c: Coincident(g89,g90)
    c: Coincident(g90,g91)
    c: Coincident(g91,g92)
    c: Coincident(g92,g89)
    c: Horizontal(g89)
    c: Horizontal(g91)
    c: Vertical(g90)
    c: Vertical(g92)
    c: Equal(g2,g91) = 30
    c: Equal(g1,g90) = 3
    c: Coincident(g74,g93)
    c: Coincident(g89,g93)
    c: Equal(g18,g93)
    c: Perpendicular(g93,g8)
    c: Coincident(g94,g95)
    c: Coincident(g95,g96)
    c: Coincident(g96,g97)
    c: Coincident(g97,g94)
    c: Horizontal(g94)
    c: Horizontal(g96)
    c: Vertical(g95)
    c: Vertical(g97)
    c: Equal(g2,g96) = 30
    c: Equal(g1,g95) = 3
    c: Coincident(g89,g98)
    c: Coincident(g94,g98)
    c: Equal(g8,g98)
    c: Parallel(g98,g8)
    c: Coincident(g99,g100)
    c: Coincident(g100,g101)
    c: Coincident(g101,g102)
    c: Coincident(g102,g99)
    c: Horizontal(g99)
    c: Horizontal(g101)
    c: Vertical(g100)
    c: Vertical(g102)
    c: Equal(g2,g101) = 30
    c: Equal(g1,g100) = 3
    c: Coincident(g94,g103)
    c: Coincident(g99,g103)
    c: Equal(g8,g103)
    c: Parallel(g103,g8)
    c: Coincident(g104,g105)
    c: Coincident(g105,g106)
    c: Coincident(g106,g107)
    c: Coincident(g107,g104)
    c: Horizontal(g104)
    c: Horizontal(g106)
    c: Vertical(g105)
    c: Vertical(g107)
    c: Equal(g2,g106) = 30
    c: Equal(g1,g105) = 3
    c: Coincident(g89,g108)
    c: Coincident(g104,g108)
    c: Equal(g18,g108)
    c: Perpendicular(g108,g8)
    c: Coincident(g109,g110)
    c: Coincident(g110,g111)
    c: Coincident(g111,g112)
    c: Coincident(g112,g109)
    c: Horizontal(g109)
    c: Horizontal(g111)
    c: Vertical(g110)
    c: Vertical(g112)
    c: Equal(g2,g111) = 30
    c: Equal(g1,g110) = 3
    c: Coincident(g104,g113)
    c: Coincident(g109,g113)
    c: Equal(g8,g113)
    c: Parallel(g113,g8)
    c: Coincident(g114,g115)
    c: Coincident(g115,g116)
    c: Coincident(g116,g117)
    c: Coincident(g117,g114)
    c: Horizontal(g114)
    c: Horizontal(g116)
    c: Vertical(g115)
    c: Vertical(g117)
    c: Equal(g2,g116) = 30
    c: Equal(g1,g115) = 3
    c: Coincident(g109,g118)
    c: Coincident(g114,g118)
    c: Equal(g8,g118)
    c: Parallel(g118,g8)
    c: Coincident(g119,g120)
    c: Coincident(g120,g121)
    c: Coincident(g121,g122)
    c: Coincident(g122,g119)
    c: Horizontal(g119)
    c: Horizontal(g121)
    c: Vertical(g120)
    c: Vertical(g122)
    c: Equal(g2,g121) = 30
    c: Equal(g1,g120) = 3
    c: Coincident(g104,g123)
    c: Coincident(g119,g123)
    c: Equal(g18,g123)
    c: Perpendicular(g123,g8)
    c: Coincident(g124,g125)
    c: Coincident(g125,g126)
    c: Coincident(g126,g127)
    c: Coincident(g127,g124)
    c: Horizontal(g124)
    c: Horizontal(g126)
    c: Vertical(g125)
    c: Vertical(g127)
    c: Equal(g2,g126) = 30
    c: Equal(g1,g125) = 3
    c: Coincident(g119,g128)
    c: Coincident(g124,g128)
    c: Equal(g8,g128)
    c: Parallel(g128,g8)
    c: Coincident(g129,g130)
    c: Coincident(g130,g131)
    c: Coincident(g131,g132)
    c: Coincident(g132,g129)
    c: Horizontal(g129)
    c: Horizontal(g131)
    c: Vertical(g130)
    c: Vertical(g132)
    c: Equal(g2,g131) = 30
    c: Equal(g1,g130) = 3
    c: Coincident(g124,g133)
    c: Coincident(g129,g133)
    c: Equal(g8,g133)
    c: Parallel(g133,g8)
    c: Coincident(g134,g135)
    c: Coincident(g135,g136)
    c: Coincident(g136,g137)
    c: Coincident(g137,g134)
    c: Horizontal(g134)
    c: Horizontal(g136)
    c: Vertical(g135)
    c: Vertical(g137)
    c: Equal(g2,g136) = 30
    c: Equal(g1,g135) = 3
    c: Coincident(g119,g138)
    c: Coincident(g134,g138)
    c: Equal(g18,g138)
    c: Perpendicular(g138,g8)
    c: Coincident(g139,g140)
    c: Coincident(g140,g141)
    c: Coincident(g141,g142)
    c: Coincident(g142,g139)
    c: Horizontal(g139)
    c: Horizontal(g141)
    c: Vertical(g140)
    c: Vertical(g142)
    c: Equal(g2,g141) = 30
    c: Equal(g1,g140) = 3
    c: Coincident(g134,g143)
    c: Coincident(g139,g143)
    c: Equal(g8,g143)
    c: Parallel(g143,g8)
    c: Coincident(g144,g145)
    c: Coincident(g145,g146)
    c: Coincident(g146,g147)
    c: Coincident(g147,g144)
    c: Horizontal(g144)
    c: Horizontal(g146)
    c: Vertical(g145)
    c: Vertical(g147)
    c: Equal(g2,g146) = 30
    c: Equal(g1,g145) = 3
    c: Coincident(g139,g148)
    c: Coincident(g144,g148)
    c: Equal(g8,g148)
    c: Parallel(g148,g8)
    c: Coincident(g149,g150)
    c: Coincident(g150,g151)
    c: Coincident(g151,g152)
    c: Coincident(g152,g149)
    c: Horizontal(g149)
    c: Horizontal(g151)
    c: Vertical(g150)
    c: Vertical(g152)
    c: Equal(g2,g151) = 30
    c: Equal(g1,g150) = 3
    c: Coincident(g134,g153)
    c: Coincident(g149,g153)
    c: Equal(g18,g153)
    c: Perpendicular(g153,g8)
    c: Coincident(g154,g155)
    c: Coincident(g155,g156)
    c: Coincident(g156,g157)
    c: Coincident(g157,g154)
    c: Horizontal(g154)
    c: Horizontal(g156)
    c: Vertical(g155)
    c: Vertical(g157)
    c: Equal(g2,g156) = 30
    c: Equal(g1,g155) = 3
    c: Coincident(g149,g158)
    c: Coincident(g154,g158)
    c: Equal(g8,g158)
    c: Parallel(g158,g8)
    c: Coincident(g159,g160)
    c: Coincident(g160,g161)
    c: Coincident(g161,g162)
    c: Coincident(g162,g159)
    c: Horizontal(g159)
    c: Horizontal(g161)
    c: Vertical(g160)
    c: Vertical(g162)
    c: Equal(g2,g161) = 30
    c: Equal(g1,g160) = 3
    c: Coincident(g154,g163)
    c: Coincident(g159,g163)
    c: Equal(g8,g163)
    c: Parallel(g163,g8)
    c: Coincident(g164,g165)
    c: Coincident(g165,g166)
    c: Coincident(g166,g167)
    c: Coincident(g167,g164)
    c: Horizontal(g164)
    c: Horizontal(g166)
    c: Vertical(g165)
    c: Vertical(g167)
    c: Equal(g2,g166) = 30
    c: Equal(g1,g165) = 3
    c: Coincident(g149,g168)
    c: Coincident(g164,g168)
    c: Equal(g18,g168)
    c: Perpendicular(g168,g8)
    c: Coincident(g169,g170)
    c: Coincident(g170,g171)
    c: Coincident(g171,g172)
    c: Coincident(g172,g169)
    c: Horizontal(g169)
    c: Horizontal(g171)
    c: Vertical(g170)
    c: Vertical(g172)
    c: Equal(g2,g171) = 30
    c: Equal(g1,g170) = 3
    c: Coincident(g164,g173)
    c: Coincident(g169,g173)
    c: Equal(g8,g173)
    c: Parallel(g173,g8)
    c: Coincident(g174,g175)
    c: Coincident(g175,g176)
    c: Coincident(g176,g177)
    c: Coincident(g177,g174)
    c: Horizontal(g174)
    c: Horizontal(g176)
    c: Vertical(g175)
    c: Vertical(g177)
    c: Equal(g2,g176) = 30
    c: Equal(g1,g175) = 3
    c: Coincident(g169,g178)
    c: Coincident(g174,g178)
    c: Equal(g8,g178)
    c: Parallel(g178,g8)
    c: Coincident(g179,g180)
    c: Coincident(g180,g181)
    c: Coincident(g181,g182)
    c: Coincident(g182,g179)
    c: Horizontal(g179)
    c: Horizontal(g181)
    c: Vertical(g180)
    c: Vertical(g182)
    c: Equal(g2,g181) = 30
    c: Equal(g1,g180) = 3
    c: Coincident(g164,g183)
    c: Coincident(g179,g183)
    c: Equal(g18,g183)
    c: Perpendicular(g183,g8)
    c: Coincident(g184,g185)
    c: Coincident(g185,g186)
    c: Coincident(g186,g187)
    c: Coincident(g187,g184)
    c: Horizontal(g184)
    c: Horizontal(g186)
    c: Vertical(g185)
    c: Vertical(g187)
    c: Equal(g2,g186) = 30
    c: Equal(g1,g185) = 3
    c: Coincident(g179,g188)
    c: Coincident(g184,g188)
    c: Equal(g8,g188)
    c: Parallel(g188,g8)
    c: Coincident(g189,g190)
    c: Coincident(g190,g191)
    c: Coincident(g191,g192)
    c: Coincident(g192,g189)
    c: Horizontal(g189)
    c: Horizontal(g191)
    c: Vertical(g190)
    c: Vertical(g192)
    c: Equal(g2,g191) = 30
    c: Equal(g1,g190) = 3
    c: Coincident(g184,g193)
    c: Coincident(g189,g193)
    c: Equal(g8,g193)
    c: Parallel(g193,g8)
    c: Coincident(g194,g195)
    c: Coincident(g195,g196)
    c: Coincident(g196,g197)
    c: Coincident(g197,g194)
    c: Horizontal(g194)
    c: Horizontal(g196)
    c: Vertical(g195)
    c: Vertical(g197)
    c: Equal(g2,g196) = 30
    c: Equal(g1,g195) = 3
    c: Coincident(g179,g198)
    c: Coincident(g194,g198)
    c: Equal(g18,g198)
    c: Perpendicular(g198,g8)
    c: Coincident(g199,g200)
    c: Coincident(g200,g201)
    c: Coincident(g201,g202)
    c: Coincident(g202,g199)
    c: Horizontal(g199)
    c: Horizontal(g201)
    c: Vertical(g200)
    c: Vertical(g202)
    c: Equal(g2,g201) = 30
    c: Equal(g1,g200) = 3
    c: Coincident(g194,g203)
    c: Coincident(g199,g203)
    c: Equal(g8,g203)
    c: Parallel(g203,g8)
    c: Coincident(g204,g205)
    c: Coincident(g205,g206)
    c: Coincident(g206,g207)
    c: Coincident(g207,g204)
    c: Horizontal(g204)
    c: Horizontal(g206)
    c: Vertical(g205)
    c: Vertical(g207)
    c: Equal(g2,g206) = 30
    c: Equal(g1,g205) = 3
    c: Coincident(g199,g208)
    c: Coincident(g204,g208)
    c: Equal(g8,g208)
    c: Parallel(g208,g8)
    c: Coincident(g209,g210)
    c: Coincident(g210,g211)
    c: Coincident(g211,g212)
    c: Coincident(g212,g209)
    c: Horizontal(g209)
    c: Horizontal(g211)
    c: Vertical(g210)
    c: Vertical(g212)
    c: Equal(g2,g211) = 30
    c: Equal(g1,g210) = 3
    c: Coincident(g194,g213)
    c: Coincident(g209,g213)
    c: Equal(g18,g213)
    c: Perpendicular(g213,g8)
    c: Coincident(g214,g215)
    c: Coincident(g215,g216)
    c: Coincident(g216,g217)
    c: Coincident(g217,g214)
    c: Horizontal(g214)
    c: Horizontal(g216)
    c: Vertical(g215)
    c: Vertical(g217)
    c: Equal(g2,g216) = 30
    c: Equal(g1,g215) = 3
    c: Coincident(g209,g218)
    c: Coincident(g214,g218)
    c: Equal(g8,g218)
    c: Parallel(g218,g8)
    c: Coincident(g219,g220)
    c: Coincident(g220,g221)
    c: Coincident(g221,g222)
    c: Coincident(g222,g219)
    c: Horizontal(g219)
    c: Horizontal(g221)
    c: Vertical(g220)
    c: Vertical(g222)
    c: Equal(g2,g221) = 30
    c: Equal(g1,g220) = 3
    c: Coincident(g214,g223)
    c: Coincident(g219,g223)
    c: Equal(g8,g223)
    c: Parallel(g223,g8)
    c: Coincident(g224,g225)
    c: Coincident(g225,g226)
    c: Coincident(g226,g227)
    c: Coincident(g227,g224)
    c: Horizontal(g224)
    c: Horizontal(g226)
    c: Vertical(g225)
    c: Vertical(g227)
    c: Equal(g2,g226) = 30
    c: Equal(g1,g225) = 3
    c: Coincident(g209,g228)
    c: Coincident(g224,g228)
    c: Equal(g18,g228)
    c: Perpendicular(g228,g8)
    c: Coincident(g229,g230)
    c: Coincident(g230,g231)
    c: Coincident(g231,g232)
    c: Coincident(g232,g229)
    c: Horizontal(g229)
    c: Horizontal(g231)
    c: Vertical(g230)
    c: Vertical(g232)
    c: Equal(g2,g231) = 30
    c: Equal(g1,g230) = 3
    c: Coincident(g224,g233)
    c: Coincident(g229,g233)
    c: Equal(g8,g233)
    c: Parallel(g233,g8)
    c: Coincident(g234,g235)
    c: Coincident(g235,g236)
    c: Coincident(g236,g237)
    c: Coincident(g237,g234)
    c: Horizontal(g234)
    c: Horizontal(g236)
    c: Vertical(g235)
    c: Vertical(g237)
    c: Equal(g2,g236) = 30
    c: Equal(g1,g235) = 3
    c: Coincident(g229,g238)
    c: Coincident(g234,g238)
    c: Equal(g8,g238)
    c: Parallel(g238,g8)
FEATURE [PartDesign::Pocket] Pocket003
  AddSubType = 1
  BaseFeature = -> Boolean001
  CheckUpToFaceLimits = true
  ClaimChildren = false
  Fit = 0
  FitJoin = 0
  InnerFit = 0
  InnerFitJoin = 0
  InnerTaperAngle = 0
  InnerTaperAngleRev = 0
  Length = 5
  Length2 = 100
  Linearize = true
  NewSolid = false
  Profile = -> Sketch009
  Suppress = false
  Type = 1
  _ProfileBasedVersion = 1
  _Version = 1
FEATURE [PartDesign::Chamfer] Chamfer001
  AddSubType = 0
  Angle = 45
  Base = -> Pocket003 [Edge16,Edge22,Edge730,Edge728,Edge767,Edge21,Edge5]
  BaseFeature = -> Pocket003
  ChamferType = 0
  FlipDirection = false
  NewSolid = false
  Size = 0.5
  Size2 = 1
  SupportTransform = false
  Suppress = false
FEATURE [PartDesign::Chamfer] Chamfer002
  AddSubType = 0
  Angle = 45
  Base = -> Chamfer001 [Edge345,Edge346,Edge84,Edge86,Edge770,Edge768,Edge766,Edge782,Edge783,Edge12,Edge7]
  BaseFeature = -> Chamfer001
  ChamferType = 0
  FlipDirection = false
  NewSolid = false
  Size = 0.95
  Size2 = 1
  SupportTransform = false
  Suppress = false
FEATURE [PartDesign::Body] Body003  label="BottomMain"
  AutoGroupSolids = false
  ExportMode = 0
  Group = -> [Pad003,Sketch007,Binder002,Boolean,Boolean001,Sketch009,Pocket003,Chamfer001,Chamfer002]
  Origin = -> Origin003
  Tip = -> Chamfer002
  _ExportChildren = -> [Pad003,Binder002,Boolean,Boolean001,Pocket003,Chamfer001,Chamfer002]
  _GroupVersion = 1
FEATURE [Mesh::Feature] Mesh  label="BottomMain (Meshed)"
FEATURE [Mesh::Feature] Mesh001  label="MainBody (Meshed)"
FEATURE [Mesh::Feature] Mesh002  label="SideDoor (Meshed)"
FEATURE [PartDesign::Body] Body  label="MainBody"
  AutoGroupSolids = false
  ExportMode = 0
  Group = -> [Sketch,Pad,Thickness,Sketch001,Pad002,LinearPattern,Sketch002,Pocket,Sketch003,Pocket001,Sketch006,Binder001,Split,Split_i0,Split_i1]
  Origin = -> Origin
  Tip = -> Split
  _ExportChildren = -> [Pad,Thickness,Pad002,LinearPattern,Pocket,Pocket001,Sketch006,Split]
  _GroupVersion = 1
FEATURE [PartDesign::Split] Split
  BaseFeature = -> Pocket001
  Fragment = false
  Mode = 0
  NewSolid = false
  Solids = -> [Split_i0,Split_i1]
  Suppress = false
  Tolerance = 0
  Tools = -> [Binder001]
  _Version = 1
FEATURE [PartDesign::Solid] Split_i0
  Active = false
  Parent = -> Split
FEATURE [PartDesign::Solid] Split_i1
  Active = true
  Parent = -> Split
